# Revit family: Internal block_22_71_DL_1R1A
name_source: partatom
category: Оборудование
units: mm (PartAtom-declared; Revit-internal decimal feet)

## family parameters
Всегда вертикально = Да
Классификация = Нет
На основе рабочей плоскости = Нет
Общий = Нет
При загрузке вырезать с полостями = Нет
Размер круглого соединителя = Использовать диаметр
Тип детали = Нормальный
Точка принадлежности помещению = Нет

## types (6) — shared parameters
00_20_Manufacturer = BLAUBERG
00_20_Name = Internal block
B = 467 мм
B1 = 224 мм
Bb = 447 мм
C = 210 мм
Casing Material = Steel, galvanized
E = 335 мм
G = 150 мм
Grid Material = Mesh, steel, painted,  white
Height = 210 мм
I = 200 мм
Load Classification = HVAC
Maintenance zone material = <По категории>
Maximum Air Flow = 0.0 л/с
Width = 467 мм
Изготовитель = BLAUBERG
zero-valued in all types: Отметка по умолчанию

## per-type parameters (varying)
| type | A | D | Db | F | H | Length | Power | Weight | d | d1 | db |
| BLHV-28-I-DL-AC/1R1A | 814 мм | 755 мм | 735 мм | 503 мм | 611 мм | 814 мм | 50 Вт | 16.00 кг | 6 мм | 10 мм | 368 мм |
| BLHV-71-I-DL-AC/1R1A | 1214 мм | 1155 мм | 1135 мм | 905 мм | 1011 мм | 1214 мм | 110 Вт | 25.50 кг | 10 мм | 16 мм | 568 мм |
| BLHV-22-I-DL-AC/1R1A | 814 мм | 755 мм | 735 мм | 503 мм | 611 мм | 814 мм | 50 Вт | 16.00 кг | 6 мм | 10 мм | 368 мм |
| BLHV-36-I-DL-AC/1R1A | 814 мм | 755 мм | 735 мм | 503 мм | 611 мм | 814 мм | 70 Вт | 16.50 кг | 6 мм | 13 мм | 368 мм |
| BLHV-45-I-DL-AC/1R1A | 814 мм | 755 мм | 735 мм | 503 мм | 611 мм | 814 мм | 80 Вт | 16.50 кг | 6 мм | 13 мм | 368 мм |
| BLHV-56-I-DL-AC/1R1A | 1010 мм | 955 мм | 935 мм | 705 мм | 811 мм | 1010 мм | 90 Вт | 21.00 кг | 6 мм | 13 мм | 468 мм |

note: column(s) folded — value = type name in every type: 00_20_Type
